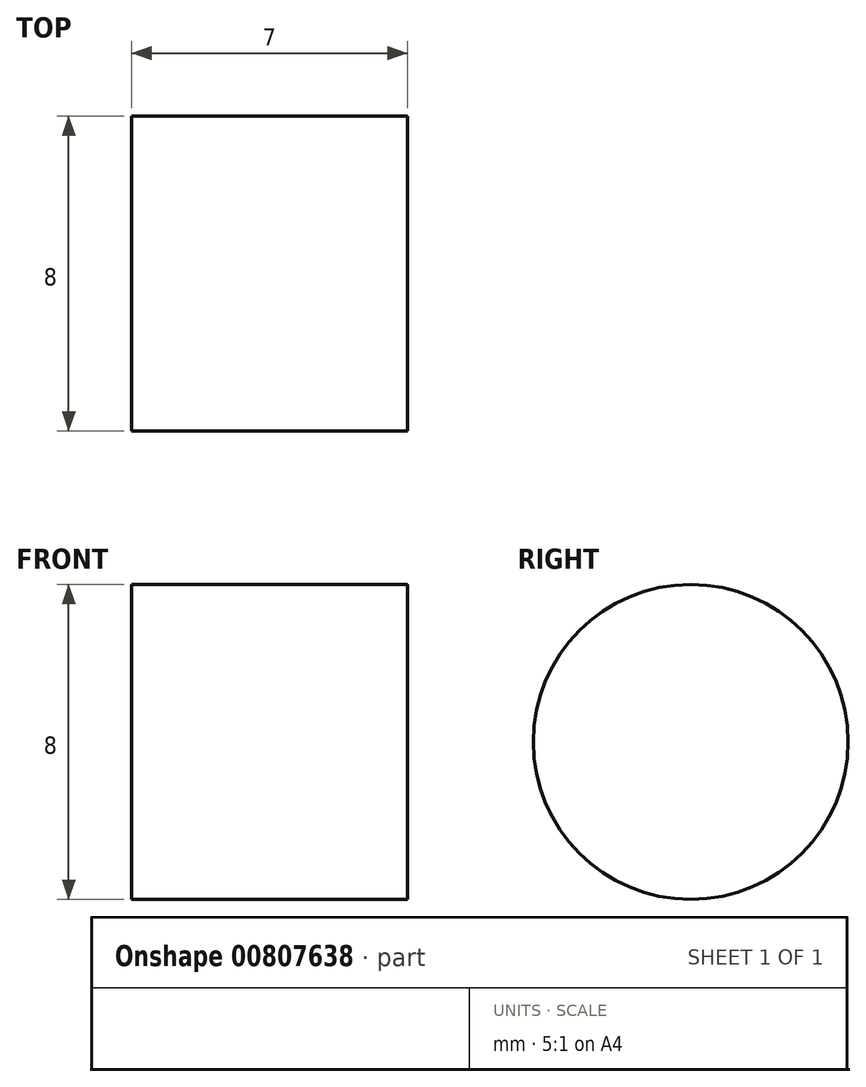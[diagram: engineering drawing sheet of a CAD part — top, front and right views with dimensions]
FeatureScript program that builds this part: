
annotation { "Feature Type Name" : "Feature", "Feature Type Description" : "" }
export const myFeature = defineFeature(function(context is Context, id is Id, definition is map)
    precondition{}
    {
        {
            var Q0;
            Q0=qCreatedBy(makeId("Right.planeOp"),FACE);
            var sketch = newSketch(context, id + "F0", { "sketchPlane" : qUnion([Q0])});
            skCircle(sketch, "E0", {"center": v(0, -0.95) * mm, "radius": 4 * mm});
            skSolve(sketch);
        }
        {
            var Q0;
            Q0 = qSketchRegion(id + "F0", true);
            extrude(context, id + "F1", {"entities" : qUnion([Q0]), "endBound" : BoundingType.SYMMETRIC, "depth" : 7 * mm, "offsetDistance" : 25 * mm});
        }
    });
